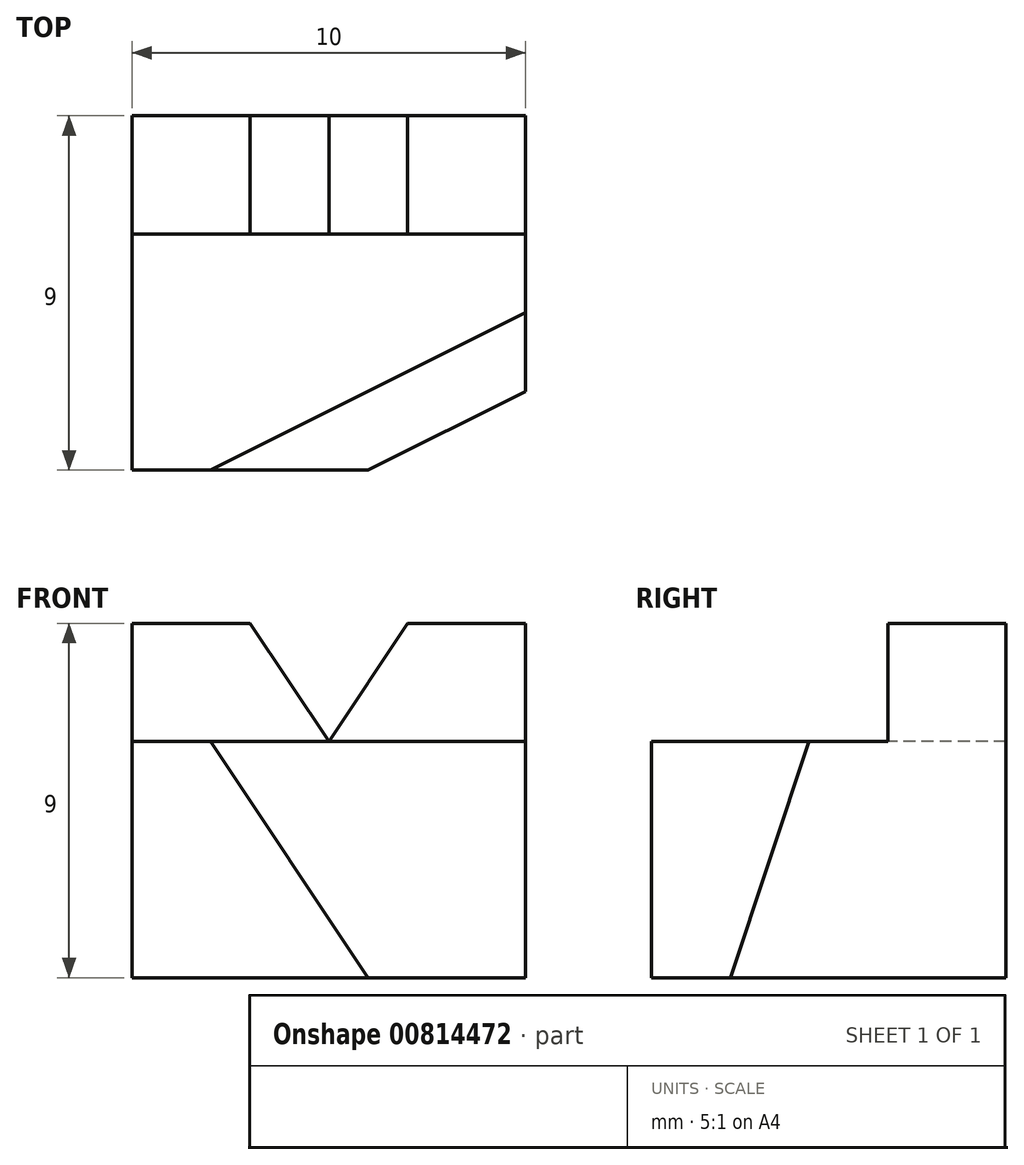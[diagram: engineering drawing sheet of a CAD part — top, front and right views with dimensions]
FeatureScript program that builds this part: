
annotation { "Feature Type Name" : "Feature", "Feature Type Description" : "" }
export const myFeature = defineFeature(function(context is Context, id is Id, definition is map)
    precondition{}
    {
        {
            var Q0;
            Q0=qCreatedBy(makeId("Right.planeOp"),FACE);
            var sketch = newSketch(context, id + "F0", { "sketchPlane" : qUnion([Q0])});
            skLineSegment(sketch, "E0.bottom", {"start": v(0, 0) * mm, "end": v(9, 0) * mm});
            skLineSegment(sketch, "E0.top", {"start": v(0, 9) * mm, "end": v(9, 9) * mm});
            skLineSegment(sketch, "E0.left", {"start": v(0, 0) * mm, "end": v(0, 9) * mm});
            skLineSegment(sketch, "E0.right", {"start": v(9, 0) * mm, "end": v(9, 9) * mm});
            skLineSegment(sketch, "E1.bottom", {"start": v(9, 9) * mm, "end": v(6, 9) * mm});
            skLineSegment(sketch, "E1.top", {"start": v(9, 6) * mm, "end": v(6, 6) * mm});
            skLineSegment(sketch, "E1.left", {"start": v(9, 9) * mm, "end": v(9, 6) * mm});
            skLineSegment(sketch, "E1.right", {"start": v(6, 9) * mm, "end": v(6, 6) * mm});
            skLineSegment(sketch, "E2", {"start": v(6, 6) * mm, "end": v(0, 6) * mm});
            skSolve(sketch);
        }
        {
            var Q0;
            {var subQ2=sQuery(id+"F0.wireOp",EDGE,"E0.bottom");Q0=makeQuery(id+"F0.imprint","IMPRINT",FACE,{"disambiguationData":[TD([[makeQuery(id+"F0.imprint","IMPRINT",EDGE,{"derivedFrom":subQ2}),1.0]])]});}
            var Q1;
            {var subQ4=sQuery(id+"F0.wireOp",EDGE,"E1.top");Q1=makeQuery(id+"F0.imprint","IMPRINT",FACE,{"disambiguationData":[TD([[makeQuery(id+"F0.imprint","IMPRINT",EDGE,{"derivedFrom":subQ4}),-1.0]])]});}
            extrude(context, id + "F1", {"entities" : qUnion([Q0, Q1]), "depth" : 10 * mm, "offsetDistance" : 25 * mm, "symmetric" : true});
        }
        {
            var Q0;
            Q0=makeQuery(id+"F1.opExtrude","CAP_FACE",FACE,{"disambiguationData":[OSD([sQuery(id+"F0.wireOp",EDGE,"E0.bottom"),sQuery(id+"F0.wireOp",EDGE,"E0.top"),sQuery(id+"F0.wireOp",EDGE,"E0.left"),sQuery(id+"F0.wireOp",EDGE,"E0.right"),sQuery(id+"F0.wireOp",EDGE,"E1.right"),sQuery(id+"F0.wireOp",EDGE,"E2")])],"isStart":false});
            var sketch = newSketch(context, id + "F2", { "sketchPlane" : qUnion([Q0])});
            skPoint(sketch, "E3", {"position": v(2, 0) * mm});
            skPoint(sketch, "E4", {"position": v(4, 6) * mm});
            skSolve(sketch);
        }
        {
            var Q0;
            Q0=makeQuery(id+"F1.opExtrude","SWEPT_FACE",FACE,{"disambiguationData":[OSD([sQuery(id+"F0.wireOp",EDGE,"E0.left")])]});
            var sketch = newSketch(context, id + "F3", { "sketchPlane" : qUnion([Q0])});
            skPoint(sketch, "E5", {"position": v(1, 0) * mm});
            skSolve(sketch);
        }
        {
            var Q0;
            Q0=sQuery(id+"F2.wireOp",VERTEX,"E4");
            var Q1;
            Q1=sQuery(id+"F2.wireOp",VERTEX,"E3");
            var Q2;
            Q2=sQuery(id+"F3.wireOp",VERTEX,"E5");
            cPlane(context, id + "F4", {"entities" : qUnion([Q0, Q1, Q2]), "cplaneType" : CPlaneType.THREE_POINT, "offset" : 25 * mm, "width" : 150 * mm, "height" : 150 * mm});
        }
        {
            var Q0;
            Q0=qCreatedBy(id+"F4.planeOp",FACE);
            var sketch = newSketch(context, id + "F5", { "sketchPlane" : qUnion([Q0])});
            skLineSegment(sketch, "E6", {"start": v(-3.52, 5.7) * mm, "end": v(5.33, 6.96) * mm});
            skLineSegment(sketch, "E7", {"start": v(5.33, -2.13) * mm, "end": v(5.33, 6.96) * mm});
            skLineSegment(sketch, "E8", {"start": v(5.33, 0.63) * mm, "end": v(0.9, 0) * mm});
            skLineSegment(sketch, "E9", {"start": v(-3.52, 5.7) * mm, "end": v(2.84, -2.48) * mm});
            skPoint(sketch, "E10.orphan", {"position": v(5.33, 0.63) * mm});
            skPoint(sketch, "E11.orphan", {"position": v(0.9, 0) * mm});
            skLineSegment(sketch, "E12", {"start": v(2.84, -2.48) * mm, "end": v(5.33, -2.13) * mm});
            skSolve(sketch);
        }
        {
            var Q0;
            Q0 = qSketchRegion(id + "F5", true);
            extrude(context, id + "F6", {"entities" : qUnion([Q0]), "operationType" : NewBodyOperationType.REMOVE, "endBound" : BoundingType.THROUGH_ALL, "depth" : 25 * mm, "offsetDistance" : 25 * mm});
        }
        {
            var Q0;
            Q0=makeQuery(id+"F1.opExtrude","SWEPT_FACE",FACE,{"disambiguationData":[OSD([sQuery(id+"F0.wireOp",EDGE,"E1.right")])]});
            var sketch = newSketch(context, id + "F7", { "sketchPlane" : qUnion([Q0])});
            skLineSegment(sketch, "E13", {"start": v(0, 0) * mm, "end": v(0, 3.3) * mm, "construction": true});
            skLineSegment(sketch, "E14", {"start": v(0, 6) * mm, "end": v(-2, 9) * mm});
            skLineSegment(sketch, "E15.MirrorCS", {"start": v(0, 6) * mm, "end": v(2, 9) * mm});
            skLineSegment(sketch, "E16.0", {"start": v(5, 9) * mm, "end": v(-5, 9) * mm});
            skSolve(sketch);
        }
        {
            var Q0;
            Q0 = qSketchRegion(id + "F7", true);
            extrude(context, id + "F8", {"entities" : qUnion([Q0]), "operationType" : NewBodyOperationType.REMOVE, "endBound" : BoundingType.THROUGH_ALL, "oppositeDirection" : true, "depth" : 25 * mm, "offsetDistance" : 25 * mm});
        }
    });
